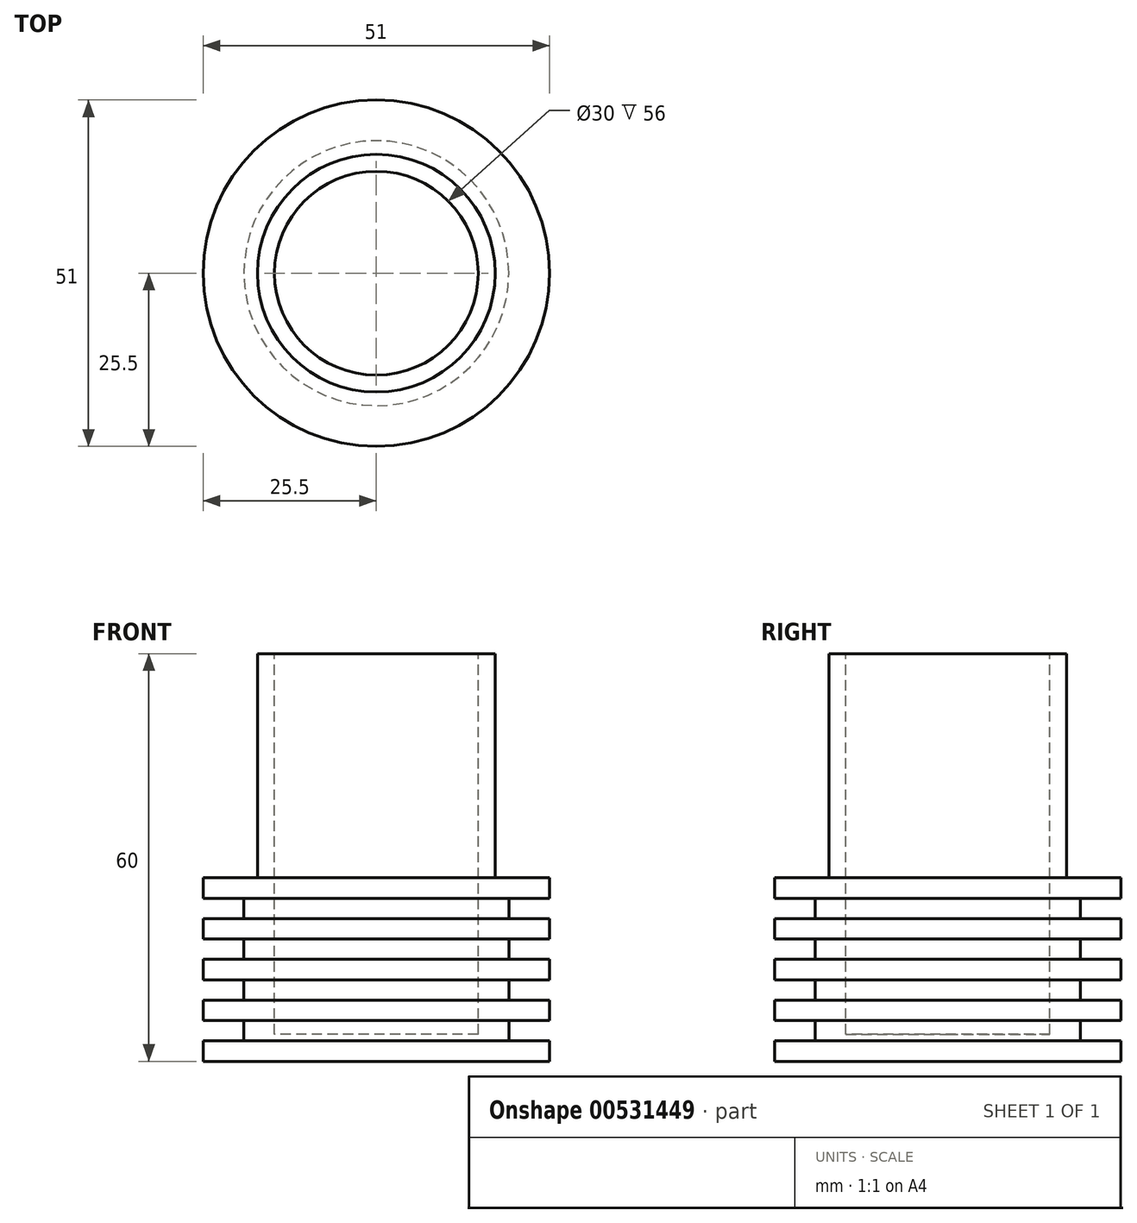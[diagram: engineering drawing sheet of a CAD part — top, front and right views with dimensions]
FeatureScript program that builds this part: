
annotation { "Feature Type Name" : "Feature", "Feature Type Description" : "" }
export const myFeature = defineFeature(function(context is Context, id is Id, definition is map)
    precondition{}
    {
        {
            var Q0;
            Q0=qCreatedBy(makeId("Top.planeOp"),FACE);
            var sketch = newSketch(context, id + "F0", { "sketchPlane" : qUnion([Q0])});
            skCircle(sketch, "E0", {"center": v(0, 0) * mm, "radius": 17.5 * mm});
            skSolve(sketch);
        }
        {
            var Q0;
            Q0 = qSketchRegion(id + "F0", true);
            extrude(context, id + "F1", {"entities" : qUnion([Q0]), "depth" : 60 * mm, "offsetDistance" : 25 * mm});
        }
        {
            var Q0;
            Q0=makeQuery(id+"F1.opExtrude","CAP_FACE",FACE,{"disambiguationData":[OSD([sQuery(id+"F0.wireOp",EDGE,"E0")])],"isStart":false});
            var sketch = newSketch(context, id + "F2", { "sketchPlane" : qUnion([Q0])});
            skCircle(sketch, "E1", {"center": v(0, 0) * mm, "radius": 15 * mm});
            skSolve(sketch);
        }
        {
            var Q0;
            Q0 = qSketchRegion(id + "F2", true);
            extrude(context, id + "F3", {"entities" : qUnion([Q0]), "operationType" : NewBodyOperationType.REMOVE, "oppositeDirection" : true, "depth" : 56 * mm, "offsetDistance" : 25 * mm});
        }
        {
            var Q0;
            Q0=qCreatedBy(makeId("Right.planeOp"),FACE);
            var sketch = newSketch(context, id + "F4", { "sketchPlane" : qUnion([Q0])});
            skLineSegment(sketch, "E2", {"start": v(-25.5, 0) * mm, "end": v(-25.5, 3) * mm});
            skLineSegment(sketch, "E3", {"start": v(-25.5, 3) * mm, "end": v(-19.5, 3) * mm});
            skLineSegment(sketch, "E4", {"start": v(-19.5, 3) * mm, "end": v(-19.5, 6) * mm});
            skLineSegment(sketch, "E5", {"start": v(-19.5, 6) * mm, "end": v(-25.5, 6) * mm});
            skLineSegment(sketch, "E6", {"start": v(-25.5, 6) * mm, "end": v(-25.5, 9) * mm});
            skLineSegment(sketch, "E7", {"start": v(-25.5, 9) * mm, "end": v(-19.5, 9) * mm});
            skLineSegment(sketch, "E8", {"start": v(-19.5, 9) * mm, "end": v(-19.5, 12) * mm});
            skLineSegment(sketch, "E9", {"start": v(-19.5, 12) * mm, "end": v(-25.5, 12) * mm});
            skLineSegment(sketch, "E10", {"start": v(-25.5, 12) * mm, "end": v(-25.5, 15) * mm});
            skLineSegment(sketch, "E11", {"start": v(-25.5, 15) * mm, "end": v(-19.5, 15) * mm});
            skLineSegment(sketch, "E12", {"start": v(-19.5, 15) * mm, "end": v(-19.5, 18) * mm});
            skLineSegment(sketch, "E13", {"start": v(-19.5, 18) * mm, "end": v(-25.5, 18) * mm});
            skLineSegment(sketch, "E14", {"start": v(-25.5, 18) * mm, "end": v(-25.5, 21) * mm});
            skLineSegment(sketch, "E15", {"start": v(-25.5, 21) * mm, "end": v(-19.5, 21) * mm});
            skLineSegment(sketch, "E16", {"start": v(-19.5, 21) * mm, "end": v(-19.5, 24) * mm});
            skLineSegment(sketch, "E17", {"start": v(-19.5, 24) * mm, "end": v(-25.5, 24) * mm});
            skLineSegment(sketch, "E18", {"start": v(-25.5, 24) * mm, "end": v(-25.5, 27) * mm});
            skLineSegment(sketch, "E19", {"start": v(-25.5, 27) * mm, "end": v(-17.5, 27) * mm});
            skLineSegment(sketch, "E20", {"start": v(-17.5, 27) * mm, "end": v(-17.5, 0) * mm});
            skLineSegment(sketch, "E21", {"start": v(-25.5, 0) * mm, "end": v(-17.5, 0) * mm});
            skLineSegment(sketch, "E22", {"start": v(0, 0) * mm, "end": v(0, 27) * mm, "construction": true});
            skSolve(sketch);
        }
        {
            var Q0;
            Q0=makeQuery(id+"F4.imprint","IMPRINT",FACE,{"disambiguationData":[TD([[makeQuery(id+"F4.imprint","IMPRINT",EDGE,{"derivedFrom":sQuery(id+"F4.wireOp",EDGE,"E2")}),-1.0]])]});
            var Q1;
            Q1=sQuery(id+"F4.wireOp",EDGE,"E22");
            revolve(context, id + "F5", {"operationType" : NewBodyOperationType.ADD, "entities" : qUnion([Q0]), "axis" : qUnion([Q1]), "revolveType" : RevolveType.FULL});
        }
    });
